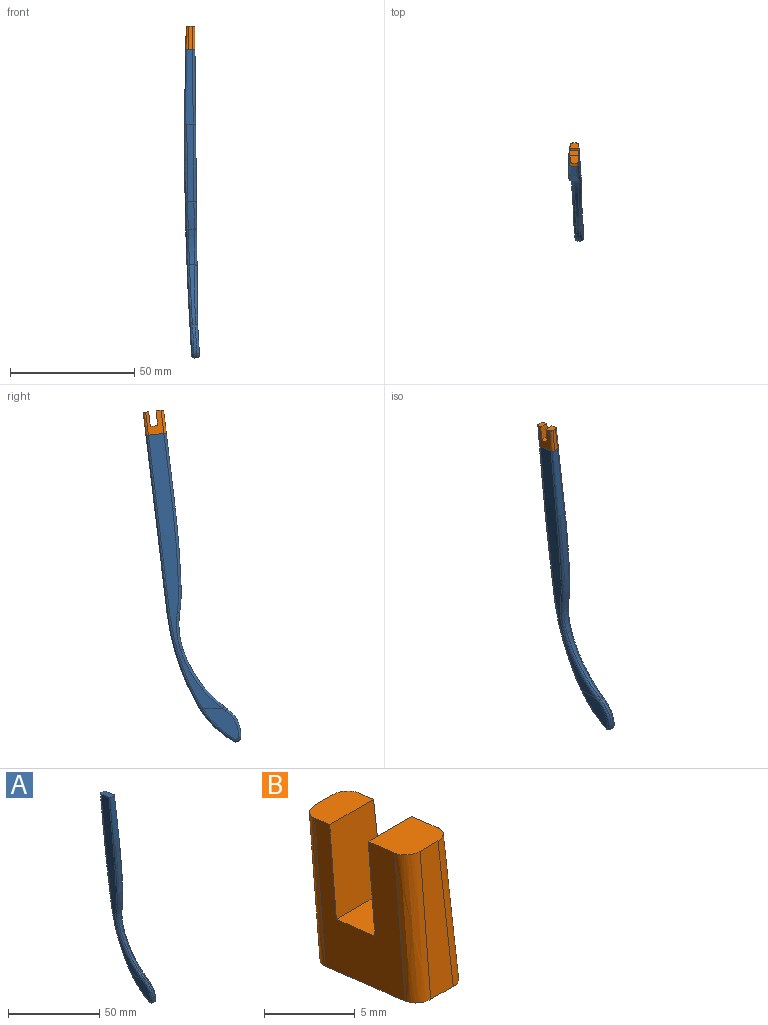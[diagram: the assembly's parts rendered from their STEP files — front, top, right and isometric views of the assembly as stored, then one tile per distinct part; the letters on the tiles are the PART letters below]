
ASSEMBLY  parts=2 mates=1
PART A: 102 faces, bbox 6.9x39.4x142.3 mm
  f0: plane 4.82x4.82mm, normal (1,0,0), area 7.2mm2, adj f39,f42,f43,f44,f45,f46,f47,f48
  f1: plane 111.14x30.19mm, normal (1,0,0.01), area 527.4mm2, adj f13,f15,f16,f17,f18,f19,f20,f33
  f2: cylinder r=1319.94mm len=110.98mm, axis (0,-1,0), area 526.6mm2, adj f14,f15,f21,f22,f23,f28,f29,f30
  f3: plane 30.2x3.59mm, normal (0,-0.99,0.12), area 66.7mm2, adj f5,f15,f20,f32
  f4: plane 71.24x8.49mm, normal (0,0.99,-0.12), area 173.5mm2, adj f12,f15,f21,f33
  f5: cylinder r=411.75mm len=31.41mm, axis (-1,0,0), area 79.9mm2, adj f3,f6,f19,f31
  f6: cylinder r=61.54mm len=10.94mm, axis (-1,0,0), area 27.2mm2, adj f5,f7,f18,f30
  f7: cylinder r=31.85mm len=14.47mm, axis (-1,0,0), area 32.5mm2, adj f6,f8,f17,f29
  f8: cylinder r=47.8mm len=24.18mm, axis (-1,0,0), area 47.5mm2, adj f7,f9,f16,f27,f28
  f9: cylinder r=12.7mm len=11.64mm, axis (-1,0,0), area 15.4mm2, adj f8,f10,f16,f26,f38
  f10: cylinder r=1.93mm len=2.91mm, axis (-1,0,0), area 4.6mm2, adj f9,f11,f25,f37
  f11: cylinder r=40.98mm len=15.15mm, axis (-1,0,0), area 24.7mm2, adj f10,f12,f23,f24,f35,f36
  f12: cylinder r=99.37mm len=36.91mm, axis (-1,0,0), area 71.1mm2, adj f4,f11,f22,f34
  f13: plane 14.81x12.83mm, normal (1,0,0.06), area 69.7mm2, adj f1,f36,f37,f38,f39
  f14: plane 14.37x12.48mm, normal (-1,0,-0.06), area 90.1mm2, adj f2,f24,f25,f26,f27,f28
  f15: plane 8.23x3.82mm, normal (0,0.12,0.99), area 30.3mm2, adj f1,f2,f3,f4,f20,f21,f32,f33
  f16: bspline ~24.99x18.91mm, area 47.3mm2, adj f1,f8,f9,f17,f38
  f17: bspline ~14.92x2.6mm, area 23.3mm2, adj f1,f7,f16,f18
  f18: bspline ~29.23x3.75mm, area 17.1mm2, adj f1,f6,f17,f19
  f19: bspline ~71.64x5.68mm, area 49.4mm2, adj f1,f5,f18,f20
  f20: cylinder r=1mm len=30.3mm, axis (-0.01,0.12,0.99), area 47.7mm2, adj f1,f3,f15,f19
  f21: bspline ~97.77x12.59mm, area 112.7mm2, adj f2,f4,f15,f22
  f22: bspline ~37x12.89mm, area 60.7mm2, adj f2,f12,f21,f23
  f23: bspline ~8.42x5.33mm, area 4.5mm2, adj f2,f11,f22,f24
  f24: bspline ~13.75x13.15mm, area 28mm2, adj f11,f14,f23,f25
  f25: bspline ~2.91x1.79mm, area 4.8mm2, adj f10,f14,f24,f26
  f26: bspline ~13.54x7.29mm, area 20.7mm2, adj f9,f14,f25,f27
  f27: bspline ~1.91x1.83mm, area 2.6mm2, adj f8,f14,f26,f28
  f28: bspline ~31.19x21.74mm, area 46.8mm2, adj f2,f8,f14,f27,f29
  f29: bspline ~22.02x3.93mm, area 23.4mm2, adj f2,f7,f28,f30
  f30: bspline ~19.6x1.88mm, area 17.1mm2, adj f2,f6,f29,f31
  f31: bspline ~71.9x6.21mm, area 49.5mm2, adj f2,f5,f30,f32
  f32: bspline ~71.59x9.48mm, area 47.7mm2, adj f2,f3,f15,f31
  f33: cylinder r=1mm len=71.34mm, axis (0.01,-0.12,-0.99), area 112.7mm2, adj f1,f4,f15,f34
  f34: bspline ~47.28x15.18mm, area 61.3mm2, adj f1,f12,f33,f35
  f35: bspline ~3.23x2.51mm, area 5mm2, adj f1,f11,f34,f36
  f36: bspline ~17.97x17.93mm, area 29.1mm2, adj f1,f11,f13,f35,f37
  f37: bspline ~2.91x1.91mm, area 5.1mm2, adj f10,f13,f36,f38
  f38: bspline ~14.16x8.7mm, area 21.1mm2, adj f1,f9,f13,f16,f37
  f39: cylinder r=2.41mm len=4.82mm, axis (1,0,0), area 20.8mm2, adj f0,f13
  f40: cylinder r=1.69mm len=2.39mm, axis (-1,0,0), area 2.7mm2, adj f41,f75,f76,f101
  f41: cylinder r=1.69mm len=2.39mm, axis (-1,0,0), area 2.7mm2, adj f40,f75,f76,f101
  f42: plane 1x0.36mm, normal (0,0,-1), area 0.4mm2, adj f0,f43,f74,f76
  f43: extruded ~1x0.33mm, area 0.4mm2, adj f0,f42,f44,f76
  f44: plane 1x0.06mm, normal (0,-0.9,-0.44), area 0.1mm2, adj f0,f43,f45,f76
  f45: plane 1x0.06mm, normal (0,0.89,-0.45), area 0.1mm2, adj f0,f44,f46,f76
  f46: extruded ~1x0.33mm, area 0.4mm2, adj f0,f45,f47,f76
  f47: cylinder r=6.28mm len=1mm, axis (-1,0,0), area 0.3mm2, adj f0,f46,f48,f76
  f48: extruded ~1x0.54mm, area 0.8mm2, adj f0,f47,f49,f76
  f49: extruded ~1x0.54mm, area 0.8mm2, adj f0,f48,f50,f76
  f50: plane 1x0.36mm, normal (0,1,0), area 0.4mm2, adj f0,f49,f51,f76
  f51: extruded ~1x0.33mm, area 0.4mm2, adj f0,f50,f52,f76
  f52: plane 1x0.06mm, normal (0,0.6,-0.8), area 0.1mm2, adj f0,f51,f53,f76
  f53: plane 1x0.06mm, normal (0,0.45,0.9), area 0.1mm2, adj f0,f52,f54,f76
  f54: extruded ~1x0.32mm, area 0.4mm2, adj f0,f53,f55,f76
  f55: cylinder r=5.58mm len=1mm, axis (-1,0,0), area 0.3mm2, adj f0,f54,f56,f76
  f56: extruded ~1x0.56mm, area 0.8mm2, adj f0,f55,f57,f76
  f57: extruded ~1x0.53mm, area 0.8mm2, adj f0,f56,f58,f76
  f58: plane 1x0.36mm, normal (0,0,1), area 0.4mm2, adj f0,f57,f59,f76
  f59: extruded ~1x0.33mm, area 0.4mm2, adj f0,f58,f60,f76
  f60: plane 1x0.05mm, normal (0,0.71,0.71), area 0.1mm2, adj f0,f59,f61,f76
  f61: plane 1x0.06mm, normal (0,-0.9,0.45), area 0.1mm2, adj f0,f60,f62,f76
  f62: extruded ~1x0.32mm, area 0.4mm2, adj f0,f61,f63,f76
  f63: cylinder r=5.83mm len=1mm, axis (-1,0,0), area 0.3mm2, adj f0,f62,f64,f76
  f64: extruded ~1x0.56mm, area 0.8mm2, adj f0,f63,f65,f76
  f65: extruded ~1x0.56mm, area 0.8mm2, adj f0,f64,f66,f76
  f66: cylinder r=5.5mm len=1mm, axis (-1,0,0), area 0.3mm2, adj f0,f65,f67,f76
  f67: extruded ~1x0.32mm, area 0.4mm2, adj f0,f66,f68,f76
  f68: plane 1x0.06mm, normal (0,-0.45,0.89), area 0.1mm2, adj f0,f67,f69,f76
  f69: plane 1x0.06mm, normal (0,-0.61,-0.8), area 0.1mm2, adj f0,f68,f70,f76
  f70: extruded ~1x0.33mm, area 0.4mm2, adj f0,f69,f71,f76
  f71: plane 1x0.36mm, normal (0,-1,0), area 0.4mm2, adj f0,f70,f72,f76
  f72: extruded ~1x0.53mm, area 0.8mm2, adj f0,f71,f73,f76
  f73: plane 1x0.02mm, normal (0,-1,0), area 0mm2, adj f0,f72,f74,f76
  f74: extruded ~1x0.54mm, area 0.8mm2, adj f0,f42,f73,f76
  f75: extruded ~2.89x2.89mm, area 5.3mm2, adj f40,f41,f76,f101
  f76: plane 4.07x4.07mm, normal (1,0,0), area 2.1mm2, adj f40,f41,f42,f43,f44,f45,f46,f47
  f77: plane 2.48x1.28mm, normal (1,0,0), area 0.8mm2, adj f79,f80,f81,f82,f83,f84,f85,f86
  f78: plane 0.99x0.95mm, normal (1,0,0), area 0.4mm2, adj f93,f94,f95,f96,f97,f98,f99,f100
  f79: cylinder r=2.64mm len=1.04mm, axis (-1,0,0), area 1.1mm2, adj f77,f80,f92,f101
  f80: plane 1x0.39mm, normal (0,-0.97,0.26), area 0.4mm2, adj f77,f79,f81,f101
  f81: plane 1x0.54mm, normal (0,0.43,0.9), area 0.6mm2, adj f77,f80,f82,f101
  f82: cylinder r=2.25mm len=1mm, axis (1,0,0), area 0.3mm2, adj f77,f81,f83,f101
  f83: cylinder r=2.15mm len=1mm, axis (1,0,0), area 0.3mm2, adj f77,f82,f84,f101
  f84: plane 1x0.54mm, normal (0,0.43,-0.9), area 0.6mm2, adj f77,f83,f85,f101
  f85: plane 1x0.39mm, normal (0,-0.97,-0.26), area 0.4mm2, adj f77,f84,f86,f101
  f86: cylinder r=2.64mm len=1.04mm, axis (-1,0,0), area 1.1mm2, adj f77,f85,f87,f101
  f87: extruded ~1x0.96mm, area 1.2mm2, adj f77,f86,f88,f101
  f88: cylinder r=2.11mm len=1mm, axis (1,0,0), area 0.8mm2, adj f77,f87,f89,f101
  f89: cylinder r=3.08mm len=1.23mm, axis (-1,0,0), area 1.3mm2, adj f77,f88,f90,f101
  f90: cylinder r=3.11mm len=1.25mm, axis (-1,0,0), area 1.3mm2, adj f77,f89,f91,f101
  f91: cylinder r=2.11mm len=1mm, axis (1,0,0), area 0.8mm2, adj f77,f90,f92,f101
  f92: extruded ~1x0.96mm, area 1.2mm2, adj f77,f79,f91,f101
  f93: plane 1x0.48mm, normal (0,0.45,0.89), area 0.5mm2, adj f78,f94,f100,f101
  f94: plane 1x0.48mm, normal (0,0.42,-0.91), area 0.5mm2, adj f78,f93,f95,f101
  f95: extruded ~1x0.24mm, area 0.2mm2, adj f78,f94,f96,f101
  f96: plane 1x0.07mm, normal (0,-0.52,0.86), area 0.1mm2, adj f78,f95,f97,f101
  f97: plane 1x0.89mm, normal (0,-0.43,0.9), area 1mm2, adj f78,f96,f98,f101
  f98: plane 1x0.89mm, normal (0,-0.44,-0.9), area 1mm2, adj f78,f97,f99,f101
  f99: plane 1x0.07mm, normal (0,-0.52,-0.86), area 0.1mm2, adj f78,f98,f100,f101
  f100: extruded ~1x0.24mm, area 0.2mm2, adj f78,f93,f99,f101
  f101: plane 3.47x3.47mm, normal (1,0,0), area 7.8mm2, adj f40,f41,f75,f79,f80,f81,f82,f83
PART B: 14 faces, bbox 4x10.7x21.9 mm
  f0: plane 5.94x3.66mm, normal (0,-0.99,0.12), area 21.2mm2, adj f1,f4,f7,f8
  f1: plane 3.66x3mm, normal (0,0.12,0.99), area 11mm2, adj f0,f2,f7,f8
  f2: plane 5.94x3.65mm, normal (0,0.99,-0.12), area 21.1mm2, adj f1,f3,f7,f8
  f3: plane 3.44x3.07mm, normal (0,0.12,0.99), area 9.9mm2, adj f2,f6,f7,f8,f10,f12
  f4: plane 3.46x2.2mm, normal (0,0.12,0.99), area 7mm2, adj f0,f5,f7,f8,f11,f13
  f5: plane 9.31x1.79mm, normal (0,0.99,-0.12), area 15.1mm2, adj f4,f9,f11,f13
  f6: plane 9.31x1.76mm, normal (0,-0.99,0.12), area 14.8mm2, adj f3,f9,f10,f12
  f7: cylinder r=1319.56mm len=10.05mm, axis (0,-1,0), area 40.6mm2, adj f0,f1,f2,f3,f4,f9,f12,f13
  f8: plane 10.05x7.31mm, normal (1,0,0.01), area 40.6mm2, adj f0,f1,f2,f3,f4,f9,f10,f11
  f9: plane 8.23x3.82mm, normal (0,-0.12,-0.99), area 30.3mm2, adj f5,f6,f7,f8,f10,f11,f12,f13
  f10: cylinder r=1mm len=9.43mm, axis (-0.01,0.12,0.99), area 14.7mm2, adj f3,f6,f8,f9
  f11: cylinder r=1mm len=9.45mm, axis (0.01,-0.12,-0.99), area 14.7mm2, adj f4,f5,f8,f9
  f12: bspline ~20.99x3.47mm, area 14.7mm2, adj f3,f6,f7,f9
  f13: bspline ~21.02x3.48mm, area 14.8mm2, adj f4,f5,f7,f9
PLACE A rot(axis=(0.45,0.65,-0.62),0deg) t=(28.41,-12.54,68.55)mm
PLACE B t=(28.41,-12.55,68.53)mm
MATE fastened B.f9 <-> A.f15  axis (0,-0.12,-0.99) through (31.31,-26.56,8.25)mm
